# Revit family: Pedestal-WashBasinFullPedestal-Vitra-MetropolSeries_4457B003-0156
name_source: partatom
category: Plumbing Fixtures
revit_build: Autodesk Revit 2017 (Build: 20160225_1515(x64)
units: mm (PartAtom-declared; Revit-internal decimal feet)

## family parameters
Cut with Voids When Loaded = No
Host = Face
OmniClass Number = 23.45.05.14.14
OmniClass Title = Sinks/Lavatories
Part Type = Normal
Room Calculation Point = No
Round Connector Dimension = Use Diameter
Shared = Yes

## types (1)
- Pedestal-WashBasinFullPedestal-Vitra-MetropolSeries_4457B003-0156
    Article No. (default) = 4457B003-0156
    BIMobject category = Sanitary - Basins
    Brand = VitrA
    CW Connection = No
    Color = White
    Cost = 0 $
    Default Elevation = 0 mm  [stored 0 ft]
    Description = VitrA Metropole
    Design country = Turkey
    HW Connection = No
    IFC Classification = Sanitary Terminal
    Main Material = Ceramic
    Manufacturer = Vitra
    Manufacturer name = Vitra
    Model = 4457B003-0156
    MountingType = Floor Mounted
    NBS Referans Code = 35-79-64
    NBS Referans Description = Pedestal Wash Basins
    Nominal Depth = 200 mm
    NominalHeight = 750 mm  [stored 2.46063 ft]
    NominalWidth = 175 mm
    OmniClass Code = 23.45.05.14.14
    OmniClass Description = Sinks/Lavatories
    Product SKU = 4457B003-0156
    Product certification = https://www.vitraglobal.com
    Product data url = https://www.vitra-bad.fr
    Product family = Floor Mounted Full Pedestal
    Product group = Metropole
    Secondary Material = Ceramic-White
    Technical description = http://cdn.vitra.com.tr
    URL = https://vitraglobal.com
    Uniclass 1.4 Code = L7212
    Uniclass 1.4 Description = Washbasins
    Uniclass 2.0 Code = PR-35-79-64
    Uniclass 2.0 Description = Pedestal Wash Basins
    Uniclass 2015 Code = Pr_40_20_96_63
    Uniclass 2015 Name = Pedestal wash basins
    Uniformat II Code = D2010
    Uniformat II Description = Plumbing Fixtures
    Vent Connection = No
    Warranty Period (Year) = 10 Years
    Waste Connection = No
    Weight Net (kg) = 13,1
    Youtube = https://www.youtube.com

note: [stored X ft] marks values corroborated as IEEE doubles in the binary element streams (Revit-internal decimal feet)

## geometry (parser evidence)
native form markers: Sweep x2
no freeform markers — native parametric forms only
